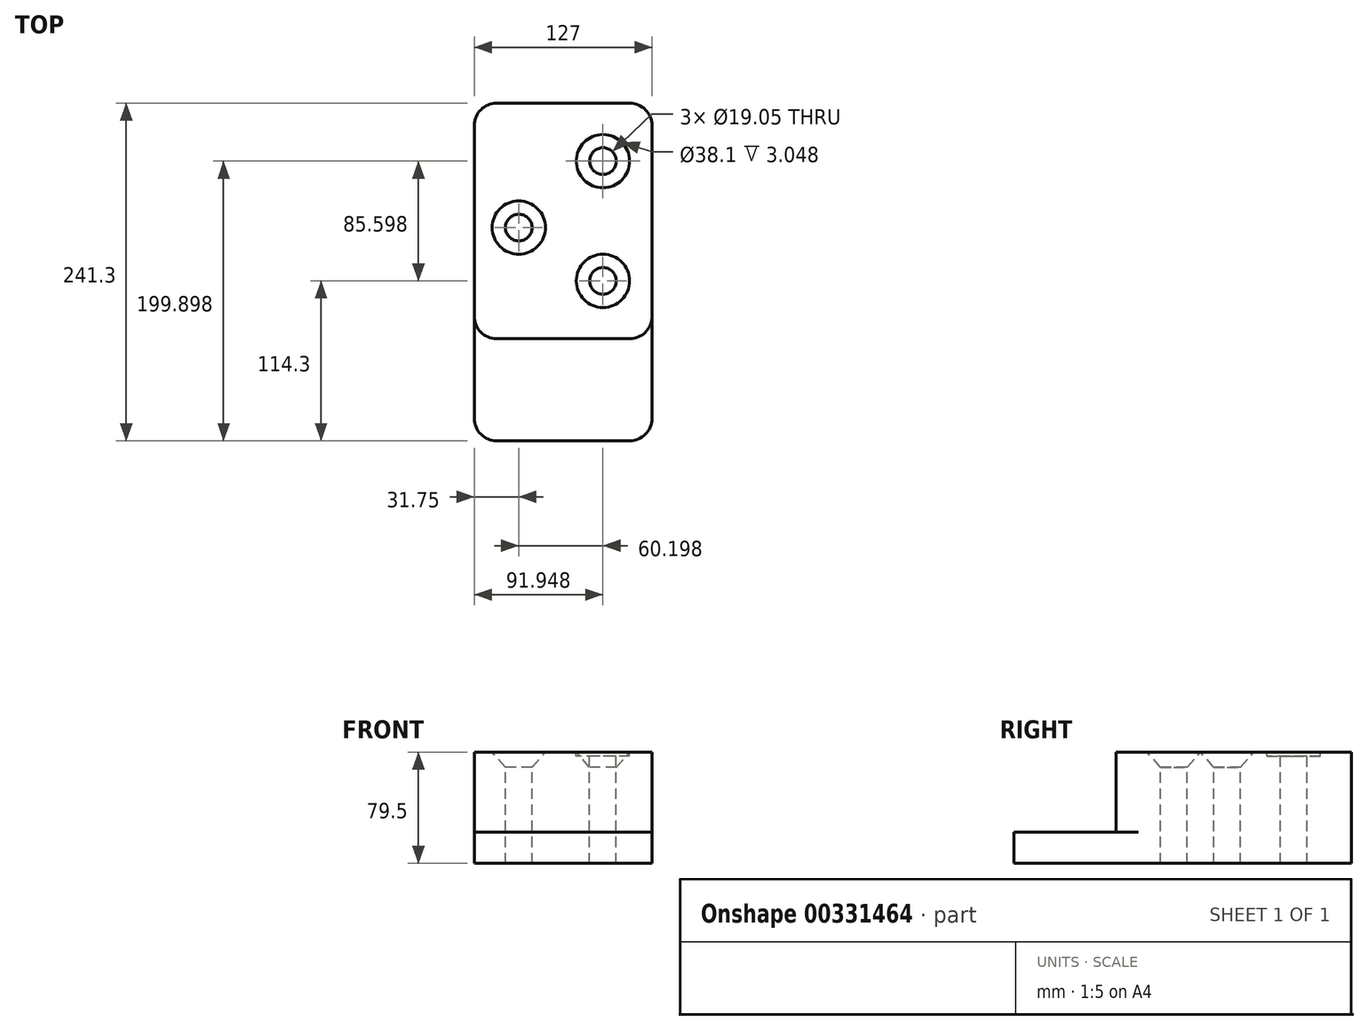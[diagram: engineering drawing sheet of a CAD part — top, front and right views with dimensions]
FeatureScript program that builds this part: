
annotation { "Feature Type Name" : "Feature", "Feature Type Description" : "" }
export const myFeature = defineFeature(function(context is Context, id is Id, definition is map)
    precondition{}
    {
        {
            var Q0;
            Q0=qCreatedBy(makeId("Top.planeOp"),FACE);
            var sketch = newSketch(context, id + "F0", { "sketchPlane" : qUnion([Q0])});
            skLineSegment(sketch, "E0.bottom", {"start": v(0, 0) * mm, "end": v(127, 0) * mm});
            skLineSegment(sketch, "E0.top", {"start": v(0, 241.3) * mm, "end": v(127, 241.3) * mm});
            skLineSegment(sketch, "E0.left", {"start": v(0, 0) * mm, "end": v(0, 241.3) * mm});
            skLineSegment(sketch, "E0.right", {"start": v(127, 0) * mm, "end": v(127, 241.3) * mm});
            skSolve(sketch);
        }
        {
            var Q0;
            Q0 = qSketchRegion(id + "F0", true);
            extrude(context, id + "F1", {"entities" : qUnion([Q0]), "depth" : 22.35 * mm});
        }
        {
            var Q0;
            Q0=makeQuery(id+"F1.opExtrude","CAP_FACE",FACE,{"disambiguationData":[OSD([sQuery(id+"F0.wireOp",EDGE,"E0.bottom"),sQuery(id+"F0.wireOp",EDGE,"E0.top"),sQuery(id+"F0.wireOp",EDGE,"E0.left"),sQuery(id+"F0.wireOp",EDGE,"E0.right")])],"isStart":false});
            var sketch = newSketch(context, id + "F2", { "sketchPlane" : qUnion([Q0])});
            skLineSegment(sketch, "E1", {"start": v(0, 72.9) * mm, "end": v(127, 72.9) * mm});
            skSolve(sketch);
        }
        {
            var Q0;
            Q0 = qSketchRegion(id + "F2", true);
            var Q1;
            {var subQ0=sQuery(id+"F2.wireOp",EDGE,"E1");Q1=makeQuery(id+"F2.imprint","IMPRINT",FACE,{"disambiguationData":[TD([[makeQuery(id+"F2.imprint","IMPRINT",EDGE,{"derivedFrom":subQ0}),1.0]])]});}
            extrude(context, id + "F3", {"entities" : qUnion([Q0, Q1]), "operationType" : NewBodyOperationType.ADD, "depth" : 57.15 * mm});
        }
        {
            var Q0;
            Q0=makeQuery(id+"F3.opExtrude","SWEPT_EDGE",EDGE,{"disambiguationData":[OSD([sQuery(id+"F0.wireOp",EDGE,"E0.right"),sQuery(id+"F2.wireOp",EDGE,"E1")])]});
            fillet(context, id + "F4", {"entities" : qUnion([Q0]), "radius" : 16 * mm, "tangentPropagation" : true, "allowEdgeOverflow" : false});
        }
        {
            var Q0;
            Q0=makeQuery(id+"F3.opExtrude","SWEPT_EDGE",EDGE,{"disambiguationData":[OSD([sQuery(id+"F0.wireOp",EDGE,"E0.left"),sQuery(id+"F2.wireOp",EDGE,"E1")])]});
            var Q1;
            Q1=makeQuery(id+"F1.opExtrude","SWEPT_EDGE",EDGE,{"disambiguationData":[OSD([sQuery(id+"F0.wireOp",EDGE,"E0.bottom"),sQuery(id+"F0.wireOp",EDGE,"E0.left")])]});
            var Q2;
            Q2=makeQuery(id+"F1.opExtrude","SWEPT_EDGE",EDGE,{"disambiguationData":[OSD([sQuery(id+"F0.wireOp",EDGE,"E0.bottom"),sQuery(id+"F0.wireOp",EDGE,"E0.right")])]});
            var Q3;
            {var subQ0=sQuery(id+"F0.wireOp",EDGE,"E0.right");var subQ1=sQuery(id+"F0.wireOp",EDGE,"E0.top");Q3=makeQuery(id+"F3.boolean.opBoolean","MERGE",EDGE,{"derivedFrom":[makeQuery(id+"F1.opExtrude","SWEPT_EDGE",EDGE,{"disambiguationData":[OSD([subQ1,subQ0])]}),makeQuery(id+"F3.opExtrude","SWEPT_EDGE",EDGE,{"disambiguationData":[OSD([subQ1,subQ0])]})]});}
            var Q4;
            {var subQ0=sQuery(id+"F0.wireOp",EDGE,"E0.left");var subQ1=sQuery(id+"F0.wireOp",EDGE,"E0.top");Q4=makeQuery(id+"F3.boolean.opBoolean","MERGE",EDGE,{"derivedFrom":[makeQuery(id+"F1.opExtrude","SWEPT_EDGE",EDGE,{"disambiguationData":[OSD([subQ1,subQ0])]}),makeQuery(id+"F3.opExtrude","SWEPT_EDGE",EDGE,{"disambiguationData":[OSD([subQ1,subQ0])]})]});}
            fillet(context, id + "F5", {"entities" : qUnion([Q0, Q1, Q2, Q3, Q4]), "radius" : 16 * mm, "tangentPropagation" : true, "allowEdgeOverflow" : false});
        }
        {
            var Q0;
            Q0=makeQuery(id+"F1.opExtrude","CAP_FACE",FACE,{"disambiguationData":[OSD([sQuery(id+"F0.wireOp",EDGE,"E0.bottom"),sQuery(id+"F0.wireOp",EDGE,"E0.top"),sQuery(id+"F0.wireOp",EDGE,"E0.left"),sQuery(id+"F0.wireOp",EDGE,"E0.right")])],"isStart":false});
            var sketch = newSketch(context, id + "F6", { "sketchPlane" : qUnion([Q0])});
            skSolve(sketch);
        }
        {
            var Q0;
            Q0=makeQuery(id+"F3.opExtrude","CAP_FACE",FACE,{"disambiguationData":[OSD([sQuery(id+"F0.wireOp",EDGE,"E0.top"),sQuery(id+"F0.wireOp",EDGE,"E0.left"),sQuery(id+"F0.wireOp",EDGE,"E0.right"),sQuery(id+"F2.wireOp",EDGE,"E1")])],"isStart":false});
            var sketch = newSketch(context, id + "F7", { "sketchPlane" : qUnion([Q0])});
            skPoint(sketch, "E2", {"position": v(91.95, 199.9) * mm});
            skPoint(sketch, "E3", {"position": v(91.95, 114.3) * mm});
            skPoint(sketch, "E4", {"position": v(31.75, 152.4) * mm});
            skSolve(sketch);
        }
        {
            var Q0;
            {var subQ0=sQuery(id+"F0.wireOp",EDGE,"E0.bottom");Q0=makeQuery(id+"F6.imprint","IMPRINT",FACE,{"disambiguationData":[TD([[makeQuery(id+"F6.imprint","IMPRINT",EDGE,{"derivedFrom":makeQuery(id+"F1.opExtrude","CAP_EDGE",EDGE,{"disambiguationData":[OSD([subQ0])],"isStart":false})}),1.0]])]});}
            var sketch = newSketch(context, id + "F8", { "sketchPlane" : qUnion([Q0])});
            skPoint(sketch, "E5", {"position": v(31.75, 35.05) * mm});
            skSolve(sketch);
        }
        {
            var Q0;
            Q0=sQuery(id+"F8.wireOp",VERTEX,"E5");
            var Q1;
            Q1=sQuery(id+"F7.wireOp",VERTEX,"E2");
            var Q2;
            Q2=makeQuery(id+"F1.opExtrude","SWEPT_BODY",BODY,{"disambiguationData":[OSD([sQuery(id+"F0.wireOp",EDGE,"E0.bottom"),sQuery(id+"F0.wireOp",EDGE,"E0.top"),sQuery(id+"F0.wireOp",EDGE,"E0.left"),sQuery(id+"F0.wireOp",EDGE,"E0.right")])]});
            hole(context, id + "F9", {"style" : HoleStyle.C_BORE, "endStyle" : HoleEndStyle.THROUGH, "holeDiameter" : 19.05 * mm, "cBoreDiameter" : 38.1 * mm, "cBoreDepth" : 3.05 * mm, "tappedDepth" : 12.7 * mm, "tapClearance" : 3, "locations" : qUnion([Q0, Q1]), "scope" : qUnion([Q2])});
        }
        {
            var Q0;
            Q0=sQuery(id+"F7.wireOp",VERTEX,"E4");
            var Q1;
            Q1=sQuery(id+"F7.wireOp",VERTEX,"E3");
            var Q2;
            Q2=makeQuery(id+"F1.opExtrude","SWEPT_BODY",BODY,{"disambiguationData":[OSD([sQuery(id+"F0.wireOp",EDGE,"E0.bottom"),sQuery(id+"F0.wireOp",EDGE,"E0.top"),sQuery(id+"F0.wireOp",EDGE,"E0.left"),sQuery(id+"F0.wireOp",EDGE,"E0.right")])]});
            hole(context, id + "F10", {"style" : HoleStyle.C_SINK, "endStyle" : HoleEndStyle.THROUGH, "holeDiameter" : 19.05 * mm, "cSinkDiameter" : 38.1 * mm, "cSinkAngle" : 82 * degree, "tappedDepth" : 12.7 * mm, "tapClearance" : 3, "locations" : qUnion([Q0, Q1]), "scope" : qUnion([Q2])});
        }
    });
